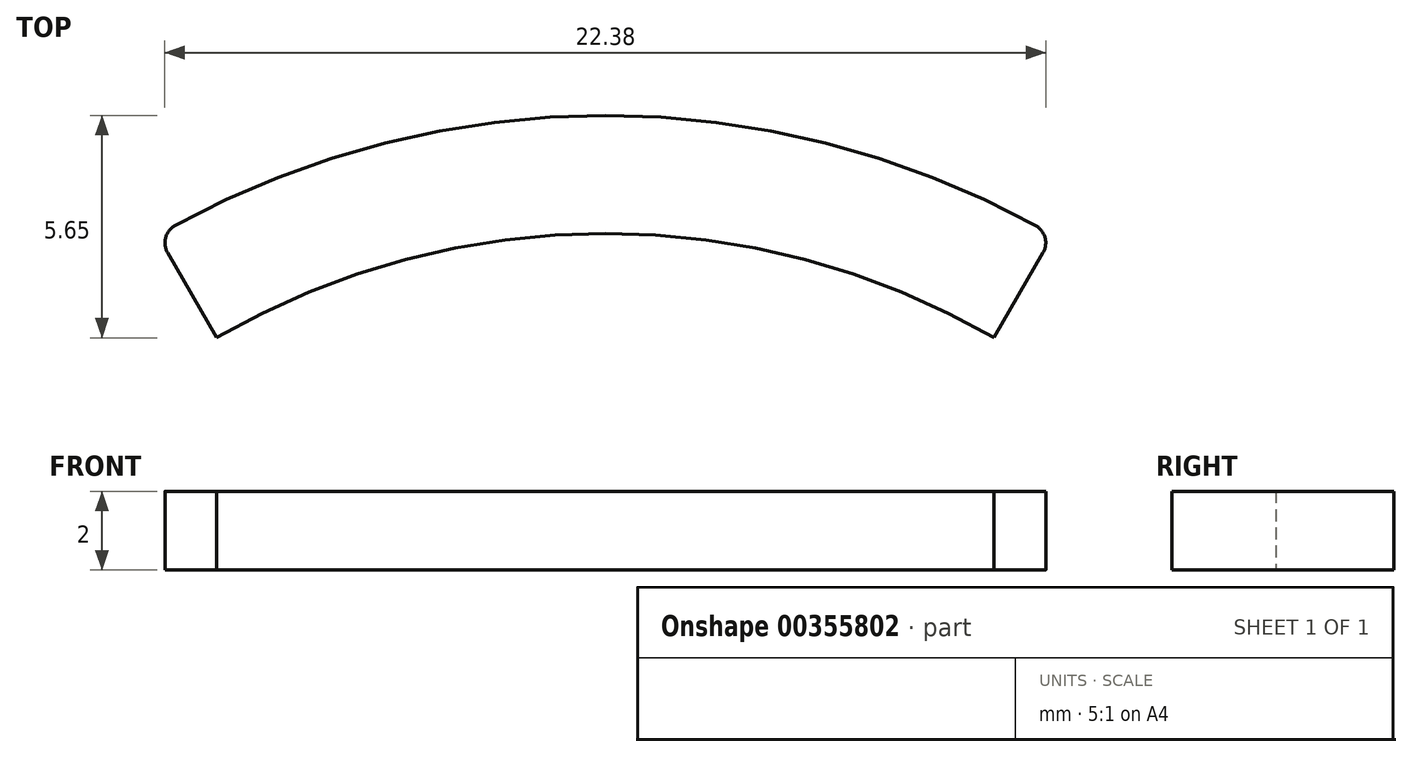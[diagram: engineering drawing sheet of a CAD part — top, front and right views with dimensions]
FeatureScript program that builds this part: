
annotation { "Feature Type Name" : "Feature", "Feature Type Description" : "" }
export const myFeature = defineFeature(function(context is Context, id is Id, definition is map)
    precondition{}
    {
        {
            var Q0;
            Q0=qCreatedBy(makeId("Top.planeOp"),FACE);
            var sketch = newSketch(context, id + "F0", { "sketchPlane" : qUnion([Q0])});
            skArc(sketch, "E0", {"start": v(9.87, 17.1) * mm, "mid": v(0, 19.75) * mm, "end": v(-9.87, 17.1) * mm});
            skArc(sketch, "E1.0", {"start": v(11.37, 19.7) * mm, "mid": v(0, 22.75) * mm, "end": v(-11.37, 19.7) * mm});
            skLineSegment(sketch, "E2", {"start": v(-9.87, 17.1) * mm, "end": v(-11.37, 19.7) * mm});
            skLineSegment(sketch, "E3", {"start": v(9.87, 17.1) * mm, "end": v(11.37, 19.7) * mm});
            skSolve(sketch);
        }
        {
            var Q0;
            Q0 = qSketchRegion(id + "F0", true);
            extrude(context, id + "F1", {"entities" : qUnion([Q0]), "depth" : 2 * mm});
        }
        {
            var Q0;
            Q0=makeQuery(id+"F1.opExtrude","SWEPT_EDGE",EDGE,{"disambiguationData":[OSD([sQuery(id+"F0.wireOp",EDGE,"E1.0"),sQuery(id+"F0.wireOp",EDGE,"E2")])]});
            var Q1;
            Q1=makeQuery(id+"F1.opExtrude","SWEPT_EDGE",EDGE,{"disambiguationData":[OSD([sQuery(id+"F0.wireOp",EDGE,"E1.0"),sQuery(id+"F0.wireOp",EDGE,"E3")])]});
            fillet(context, id + "F2", {"entities" : qUnion([Q0, Q1]), "radius" : .5 * mm, "tangentPropagation" : true, "allowEdgeOverflow" : false});
        }
    });
